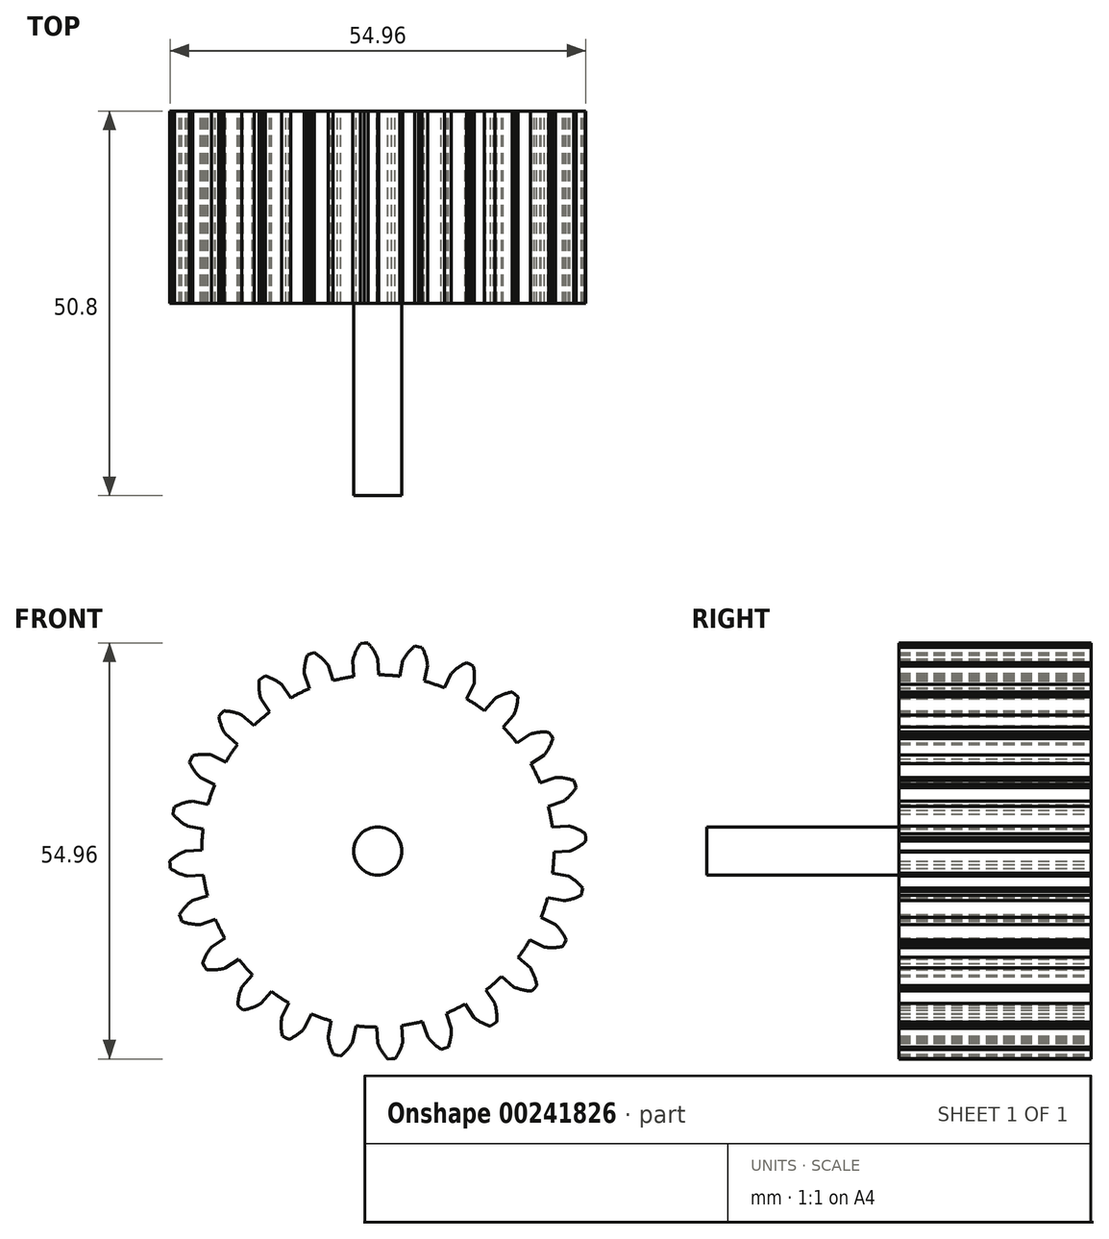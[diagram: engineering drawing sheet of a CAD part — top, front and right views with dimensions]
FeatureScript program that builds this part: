
annotation { "Feature Type Name" : "Feature", "Feature Type Description" : "" }
export const myFeature = defineFeature(function(context is Context, id is Id, definition is map)
    precondition{}
    {
        {
            var Q0;
            Q0=qCreatedBy(makeId("Front.planeOp"),FACE);
            var sketch = newSketch(context, id + "F0", { "sketchPlane" : qUnion([Q0])});
            skCircle(sketch, "E0", {"center": v(0, 0) * mm, "radius": 23.28 * mm});
            skArc(sketch, "E1.trimOffspring", {"start": v(0, 25.4) * mm, "mid": v(-0.55, 26.5) * mm, "end": v(-1.31, 27.48) * mm});
            skLineSegment(sketch, "E2", {"start": v(0, 25.4) * mm, "end": v(0.14, 23.28) * mm});
            skLineSegment(sketch, "E3", {"start": v(-1.31, 27.48) * mm, "end": v(-1.8, 27.46) * mm});
            skLineSegment(sketch, "E4.MirrorCS", {"start": v(-2.28, 27.42) * mm, "end": v(-1.8, 27.46) * mm});
            skArc(sketch, "E5.MirrorCS", {"start": v(-3.32, 25.18) * mm, "mid": v(-2.9, 26.35) * mm, "end": v(-2.28, 27.42) * mm});
            skLineSegment(sketch, "E6.MirrorCS", {"start": v(-3.32, 25.18) * mm, "end": v(-3.18, 23.07) * mm});
            skPoint(sketch, "E7.orphan", {"position": v(-3.01, 20.57) * mm});
            skPoint(sketch, "E8.orphan", {"position": v(0.3, 20.78) * mm});
            skLineSegment(sketch, "E9.1.0", {"start": v(-9.72, 23.47) * mm, "end": v(-9.04, 21.46) * mm});
            skArc(sketch, "E9.1.1", {"start": v(-9.72, 23.47) * mm, "mid": v(-9.63, 24.7) * mm, "end": v(-9.3, 25.9) * mm});
            skLineSegment(sketch, "E9.1.2", {"start": v(-9.3, 25.9) * mm, "end": v(-8.85, 26.06) * mm});
            skLineSegment(sketch, "E9.1.3", {"start": v(-8.38, 26.2) * mm, "end": v(-8.85, 26.06) * mm});
            skArc(sketch, "E9.1.4", {"start": v(-6.57, 24.53) * mm, "mid": v(-7.4, 25.46) * mm, "end": v(-8.38, 26.2) * mm});
            skLineSegment(sketch, "E9.1.5", {"start": v(-6.57, 24.53) * mm, "end": v(-5.9, 22.53) * mm});
            skLineSegment(sketch, "E9.2.0", {"start": v(-15.46, 20.15) * mm, "end": v(-14.28, 18.39) * mm});
            skArc(sketch, "E9.2.1", {"start": v(-15.46, 20.15) * mm, "mid": v(-15.7, 21.37) * mm, "end": v(-15.69, 22.6) * mm});
            skLineSegment(sketch, "E9.2.2", {"start": v(-15.69, 22.6) * mm, "end": v(-15.29, 22.88) * mm});
            skLineSegment(sketch, "E9.2.3", {"start": v(-14.88, 23.15) * mm, "end": v(-15.29, 22.88) * mm});
            skArc(sketch, "E9.2.4", {"start": v(-12.7, 22) * mm, "mid": v(-13.73, 22.68) * mm, "end": v(-14.88, 23.15) * mm});
            skLineSegment(sketch, "E9.2.5", {"start": v(-12.7, 22) * mm, "end": v(-11.52, 20.23) * mm});
            skLineSegment(sketch, "E9.3.0", {"start": v(-20.15, 15.46) * mm, "end": v(-18.56, 14.06) * mm});
            skArc(sketch, "E9.3.1", {"start": v(-20.15, 15.46) * mm, "mid": v(-20.7, 16.58) * mm, "end": v(-21, 17.77) * mm});
            skLineSegment(sketch, "E9.3.2", {"start": v(-21, 17.77) * mm, "end": v(-20.7, 18.15) * mm});
            skLineSegment(sketch, "E9.3.3", {"start": v(-20.36, 18.5) * mm, "end": v(-20.7, 18.15) * mm});
            skArc(sketch, "E9.3.4", {"start": v(-17.96, 17.96) * mm, "mid": v(-19.14, 18.35) * mm, "end": v(-20.36, 18.5) * mm});
            skLineSegment(sketch, "E9.3.5", {"start": v(-17.96, 17.96) * mm, "end": v(-16.37, 16.56) * mm});
            skLineSegment(sketch, "E9.4.0", {"start": v(-23.47, 9.72) * mm, "end": v(-21.56, 8.78) * mm});
            skArc(sketch, "E9.4.1", {"start": v(-23.47, 9.72) * mm, "mid": v(-24.28, 10.66) * mm, "end": v(-24.89, 11.73) * mm});
            skLineSegment(sketch, "E9.4.2", {"start": v(-24.89, 11.73) * mm, "end": v(-24.68, 12.17) * mm});
            skLineSegment(sketch, "E9.4.3", {"start": v(-24.46, 12.6) * mm, "end": v(-24.68, 12.17) * mm});
            skArc(sketch, "E9.4.4", {"start": v(-22, 12.7) * mm, "mid": v(-23.23, 12.77) * mm, "end": v(-24.46, 12.6) * mm});
            skLineSegment(sketch, "E9.4.5", {"start": v(-22, 12.7) * mm, "end": v(-20.1, 11.76) * mm});
            skLineSegment(sketch, "E9.5.0", {"start": v(-25.18, 3.32) * mm, "end": v(-23.1, 2.9) * mm});
            skArc(sketch, "E9.5.1", {"start": v(-25.18, 3.32) * mm, "mid": v(-26.2, 4) * mm, "end": v(-27.08, 4.9) * mm});
            skLineSegment(sketch, "E9.5.2", {"start": v(-27.08, 4.9) * mm, "end": v(-27, 5.37) * mm});
            skLineSegment(sketch, "E9.5.3", {"start": v(-26.89, 5.84) * mm, "end": v(-27, 5.37) * mm});
            skArc(sketch, "E9.5.4", {"start": v(-24.53, 6.57) * mm, "mid": v(-25.75, 6.32) * mm, "end": v(-26.89, 5.84) * mm});
            skLineSegment(sketch, "E9.5.5", {"start": v(-24.53, 6.57) * mm, "end": v(-22.45, 6.16) * mm});
            skLineSegment(sketch, "E9.6.0", {"start": v(-25.18, -3.32) * mm, "end": v(-23.07, -3.18) * mm});
            skArc(sketch, "E9.6.1", {"start": v(-25.18, -3.32) * mm, "mid": v(-26.35, -2.9) * mm, "end": v(-27.42, -2.28) * mm});
            skLineSegment(sketch, "E9.6.2", {"start": v(-27.42, -2.28) * mm, "end": v(-27.46, -1.8) * mm});
            skLineSegment(sketch, "E9.6.3", {"start": v(-27.48, -1.31) * mm, "end": v(-27.46, -1.8) * mm});
            skArc(sketch, "E9.6.4", {"start": v(-25.4, 0) * mm, "mid": v(-26.5, -0.55) * mm, "end": v(-27.48, -1.31) * mm});
            skLineSegment(sketch, "E9.6.5", {"start": v(-25.4, 0) * mm, "end": v(-23.28, 0.14) * mm});
            skLineSegment(sketch, "E9.7.0", {"start": v(-23.47, -9.72) * mm, "end": v(-21.46, -9.04) * mm});
            skArc(sketch, "E9.7.1", {"start": v(-23.47, -9.72) * mm, "mid": v(-24.7, -9.63) * mm, "end": v(-25.9, -9.3) * mm});
            skLineSegment(sketch, "E9.7.2", {"start": v(-25.9, -9.3) * mm, "end": v(-26.06, -8.85) * mm});
            skLineSegment(sketch, "E9.7.3", {"start": v(-26.2, -8.38) * mm, "end": v(-26.06, -8.85) * mm});
            skArc(sketch, "E9.7.4", {"start": v(-24.53, -6.57) * mm, "mid": v(-25.46, -7.4) * mm, "end": v(-26.2, -8.38) * mm});
            skLineSegment(sketch, "E9.7.5", {"start": v(-24.53, -6.57) * mm, "end": v(-22.53, -5.9) * mm});
            skLineSegment(sketch, "E9.8.0", {"start": v(-20.15, -15.46) * mm, "end": v(-18.39, -14.28) * mm});
            skArc(sketch, "E9.8.1", {"start": v(-20.15, -15.46) * mm, "mid": v(-21.37, -15.7) * mm, "end": v(-22.6, -15.69) * mm});
            skLineSegment(sketch, "E9.8.2", {"start": v(-22.6, -15.69) * mm, "end": v(-22.88, -15.29) * mm});
            skLineSegment(sketch, "E9.8.3", {"start": v(-23.15, -14.88) * mm, "end": v(-22.88, -15.29) * mm});
            skArc(sketch, "E9.8.4", {"start": v(-22, -12.7) * mm, "mid": v(-22.68, -13.73) * mm, "end": v(-23.15, -14.88) * mm});
            skLineSegment(sketch, "E9.8.5", {"start": v(-22, -12.7) * mm, "end": v(-20.23, -11.52) * mm});
            skLineSegment(sketch, "E9.9.0", {"start": v(-15.46, -20.15) * mm, "end": v(-14.06, -18.56) * mm});
            skArc(sketch, "E9.9.1", {"start": v(-15.46, -20.15) * mm, "mid": v(-16.58, -20.7) * mm, "end": v(-17.77, -21) * mm});
            skLineSegment(sketch, "E9.9.2", {"start": v(-17.77, -21) * mm, "end": v(-18.15, -20.7) * mm});
            skLineSegment(sketch, "E9.9.3", {"start": v(-18.5, -20.36) * mm, "end": v(-18.15, -20.7) * mm});
            skArc(sketch, "E9.9.4", {"start": v(-17.96, -17.96) * mm, "mid": v(-18.35, -19.14) * mm, "end": v(-18.5, -20.36) * mm});
            skLineSegment(sketch, "E9.9.5", {"start": v(-17.96, -17.96) * mm, "end": v(-16.56, -16.37) * mm});
            skLineSegment(sketch, "E9.10.0", {"start": v(-9.72, -23.47) * mm, "end": v(-8.78, -21.56) * mm});
            skArc(sketch, "E9.10.1", {"start": v(-9.72, -23.47) * mm, "mid": v(-10.66, -24.28) * mm, "end": v(-11.73, -24.89) * mm});
            skLineSegment(sketch, "E9.10.2", {"start": v(-11.73, -24.89) * mm, "end": v(-12.17, -24.68) * mm});
            skLineSegment(sketch, "E9.10.3", {"start": v(-12.6, -24.46) * mm, "end": v(-12.17, -24.68) * mm});
            skArc(sketch, "E9.10.4", {"start": v(-12.7, -22) * mm, "mid": v(-12.77, -23.23) * mm, "end": v(-12.6, -24.46) * mm});
            skLineSegment(sketch, "E9.10.5", {"start": v(-12.7, -22) * mm, "end": v(-11.76, -20.1) * mm});
            skLineSegment(sketch, "E9.11.0", {"start": v(-3.32, -25.18) * mm, "end": v(-2.9, -23.1) * mm});
            skArc(sketch, "E9.11.1", {"start": v(-3.32, -25.18) * mm, "mid": v(-4, -26.2) * mm, "end": v(-4.9, -27.08) * mm});
            skLineSegment(sketch, "E9.11.2", {"start": v(-4.9, -27.08) * mm, "end": v(-5.37, -27) * mm});
            skLineSegment(sketch, "E9.11.3", {"start": v(-5.84, -26.89) * mm, "end": v(-5.37, -27) * mm});
            skArc(sketch, "E9.11.4", {"start": v(-6.57, -24.53) * mm, "mid": v(-6.32, -25.75) * mm, "end": v(-5.84, -26.89) * mm});
            skLineSegment(sketch, "E9.11.5", {"start": v(-6.57, -24.53) * mm, "end": v(-6.16, -22.45) * mm});
            skLineSegment(sketch, "E9.12.0", {"start": v(3.32, -25.18) * mm, "end": v(3.18, -23.07) * mm});
            skArc(sketch, "E9.12.1", {"start": v(3.32, -25.18) * mm, "mid": v(2.9, -26.35) * mm, "end": v(2.28, -27.42) * mm});
            skLineSegment(sketch, "E9.12.2", {"start": v(2.28, -27.42) * mm, "end": v(1.8, -27.46) * mm});
            skLineSegment(sketch, "E9.12.3", {"start": v(1.31, -27.48) * mm, "end": v(1.8, -27.46) * mm});
            skArc(sketch, "E9.12.4", {"start": v(0, -25.4) * mm, "mid": v(0.55, -26.5) * mm, "end": v(1.31, -27.48) * mm});
            skLineSegment(sketch, "E9.12.5", {"start": v(0, -25.4) * mm, "end": v(-0.14, -23.28) * mm});
            skLineSegment(sketch, "E9.13.0", {"start": v(9.72, -23.47) * mm, "end": v(9.04, -21.46) * mm});
            skArc(sketch, "E9.13.1", {"start": v(9.72, -23.47) * mm, "mid": v(9.63, -24.7) * mm, "end": v(9.3, -25.9) * mm});
            skLineSegment(sketch, "E9.13.2", {"start": v(9.3, -25.9) * mm, "end": v(8.85, -26.06) * mm});
            skLineSegment(sketch, "E9.13.3", {"start": v(8.38, -26.2) * mm, "end": v(8.85, -26.06) * mm});
            skArc(sketch, "E9.13.4", {"start": v(6.57, -24.53) * mm, "mid": v(7.4, -25.46) * mm, "end": v(8.38, -26.2) * mm});
            skLineSegment(sketch, "E9.13.5", {"start": v(6.57, -24.53) * mm, "end": v(5.9, -22.53) * mm});
            skLineSegment(sketch, "E9.14.0", {"start": v(15.46, -20.15) * mm, "end": v(14.28, -18.39) * mm});
            skArc(sketch, "E9.14.1", {"start": v(15.46, -20.15) * mm, "mid": v(15.7, -21.37) * mm, "end": v(15.69, -22.6) * mm});
            skLineSegment(sketch, "E9.14.2", {"start": v(15.69, -22.6) * mm, "end": v(15.29, -22.88) * mm});
            skLineSegment(sketch, "E9.14.3", {"start": v(14.88, -23.15) * mm, "end": v(15.29, -22.88) * mm});
            skArc(sketch, "E9.14.4", {"start": v(12.7, -22) * mm, "mid": v(13.73, -22.68) * mm, "end": v(14.88, -23.15) * mm});
            skLineSegment(sketch, "E9.14.5", {"start": v(12.7, -22) * mm, "end": v(11.52, -20.23) * mm});
            skLineSegment(sketch, "E9.15.0", {"start": v(20.15, -15.46) * mm, "end": v(18.56, -14.06) * mm});
            skArc(sketch, "E9.15.1", {"start": v(20.15, -15.46) * mm, "mid": v(20.7, -16.58) * mm, "end": v(21, -17.77) * mm});
            skLineSegment(sketch, "E9.15.2", {"start": v(21, -17.77) * mm, "end": v(20.7, -18.15) * mm});
            skLineSegment(sketch, "E9.15.3", {"start": v(20.36, -18.5) * mm, "end": v(20.7, -18.15) * mm});
            skArc(sketch, "E9.15.4", {"start": v(17.96, -17.96) * mm, "mid": v(19.14, -18.35) * mm, "end": v(20.36, -18.5) * mm});
            skLineSegment(sketch, "E9.15.5", {"start": v(17.96, -17.96) * mm, "end": v(16.37, -16.56) * mm});
            skLineSegment(sketch, "E9.16.0", {"start": v(23.47, -9.72) * mm, "end": v(21.56, -8.78) * mm});
            skArc(sketch, "E9.16.1", {"start": v(23.47, -9.72) * mm, "mid": v(24.28, -10.66) * mm, "end": v(24.89, -11.73) * mm});
            skLineSegment(sketch, "E9.16.2", {"start": v(24.89, -11.73) * mm, "end": v(24.68, -12.17) * mm});
            skLineSegment(sketch, "E9.16.3", {"start": v(24.46, -12.6) * mm, "end": v(24.68, -12.17) * mm});
            skArc(sketch, "E9.16.4", {"start": v(22, -12.7) * mm, "mid": v(23.23, -12.77) * mm, "end": v(24.46, -12.6) * mm});
            skLineSegment(sketch, "E9.16.5", {"start": v(22, -12.7) * mm, "end": v(20.1, -11.76) * mm});
            skLineSegment(sketch, "E9.17.0", {"start": v(25.18, -3.32) * mm, "end": v(23.1, -2.9) * mm});
            skArc(sketch, "E9.17.1", {"start": v(25.18, -3.32) * mm, "mid": v(26.2, -4) * mm, "end": v(27.08, -4.9) * mm});
            skLineSegment(sketch, "E9.17.2", {"start": v(27.08, -4.9) * mm, "end": v(27, -5.37) * mm});
            skLineSegment(sketch, "E9.17.3", {"start": v(26.89, -5.84) * mm, "end": v(27, -5.37) * mm});
            skArc(sketch, "E9.17.4", {"start": v(24.53, -6.57) * mm, "mid": v(25.75, -6.32) * mm, "end": v(26.89, -5.84) * mm});
            skLineSegment(sketch, "E9.17.5", {"start": v(24.53, -6.57) * mm, "end": v(22.45, -6.16) * mm});
            skLineSegment(sketch, "E9.18.0", {"start": v(25.18, 3.32) * mm, "end": v(23.07, 3.18) * mm});
            skArc(sketch, "E9.18.1", {"start": v(25.18, 3.32) * mm, "mid": v(26.35, 2.9) * mm, "end": v(27.42, 2.28) * mm});
            skLineSegment(sketch, "E9.18.2", {"start": v(27.42, 2.28) * mm, "end": v(27.46, 1.8) * mm});
            skLineSegment(sketch, "E9.18.3", {"start": v(27.48, 1.31) * mm, "end": v(27.46, 1.8) * mm});
            skArc(sketch, "E9.18.4", {"start": v(25.4, 0) * mm, "mid": v(26.5, 0.55) * mm, "end": v(27.48, 1.31) * mm});
            skLineSegment(sketch, "E9.18.5", {"start": v(25.4, 0) * mm, "end": v(23.28, -0.14) * mm});
            skLineSegment(sketch, "E9.19.0", {"start": v(23.47, 9.72) * mm, "end": v(21.46, 9.04) * mm});
            skArc(sketch, "E9.19.1", {"start": v(23.47, 9.72) * mm, "mid": v(24.7, 9.63) * mm, "end": v(25.9, 9.3) * mm});
            skLineSegment(sketch, "E9.19.2", {"start": v(25.9, 9.3) * mm, "end": v(26.06, 8.85) * mm});
            skLineSegment(sketch, "E9.19.3", {"start": v(26.2, 8.38) * mm, "end": v(26.06, 8.85) * mm});
            skArc(sketch, "E9.19.4", {"start": v(24.53, 6.57) * mm, "mid": v(25.46, 7.4) * mm, "end": v(26.2, 8.38) * mm});
            skLineSegment(sketch, "E9.19.5", {"start": v(24.53, 6.57) * mm, "end": v(22.53, 5.9) * mm});
            skLineSegment(sketch, "E9.20.0", {"start": v(20.15, 15.46) * mm, "end": v(18.39, 14.28) * mm});
            skArc(sketch, "E9.20.1", {"start": v(20.15, 15.46) * mm, "mid": v(21.37, 15.7) * mm, "end": v(22.6, 15.69) * mm});
            skLineSegment(sketch, "E9.20.2", {"start": v(22.6, 15.69) * mm, "end": v(22.88, 15.29) * mm});
            skLineSegment(sketch, "E9.20.3", {"start": v(23.15, 14.88) * mm, "end": v(22.88, 15.29) * mm});
            skArc(sketch, "E9.20.4", {"start": v(22, 12.7) * mm, "mid": v(22.68, 13.73) * mm, "end": v(23.15, 14.88) * mm});
            skLineSegment(sketch, "E9.20.5", {"start": v(22, 12.7) * mm, "end": v(20.23, 11.52) * mm});
            skLineSegment(sketch, "E9.21.0", {"start": v(15.46, 20.15) * mm, "end": v(14.06, 18.56) * mm});
            skArc(sketch, "E9.21.1", {"start": v(15.46, 20.15) * mm, "mid": v(16.58, 20.7) * mm, "end": v(17.77, 21) * mm});
            skLineSegment(sketch, "E9.21.2", {"start": v(17.77, 21) * mm, "end": v(18.15, 20.7) * mm});
            skLineSegment(sketch, "E9.21.3", {"start": v(18.5, 20.36) * mm, "end": v(18.15, 20.7) * mm});
            skArc(sketch, "E9.21.4", {"start": v(17.96, 17.96) * mm, "mid": v(18.35, 19.14) * mm, "end": v(18.5, 20.36) * mm});
            skLineSegment(sketch, "E9.21.5", {"start": v(17.96, 17.96) * mm, "end": v(16.56, 16.37) * mm});
            skLineSegment(sketch, "E9.22.0", {"start": v(9.72, 23.47) * mm, "end": v(8.78, 21.56) * mm});
            skArc(sketch, "E9.22.1", {"start": v(9.72, 23.47) * mm, "mid": v(10.66, 24.28) * mm, "end": v(11.73, 24.89) * mm});
            skLineSegment(sketch, "E9.22.2", {"start": v(11.73, 24.89) * mm, "end": v(12.17, 24.68) * mm});
            skLineSegment(sketch, "E9.22.3", {"start": v(12.6, 24.46) * mm, "end": v(12.17, 24.68) * mm});
            skArc(sketch, "E9.22.4", {"start": v(12.7, 22) * mm, "mid": v(12.77, 23.23) * mm, "end": v(12.6, 24.46) * mm});
            skLineSegment(sketch, "E9.22.5", {"start": v(12.7, 22) * mm, "end": v(11.76, 20.1) * mm});
            skLineSegment(sketch, "E9.23.0", {"start": v(3.32, 25.18) * mm, "end": v(2.9, 23.1) * mm});
            skArc(sketch, "E9.23.1", {"start": v(3.32, 25.18) * mm, "mid": v(4, 26.2) * mm, "end": v(4.9, 27.08) * mm});
            skLineSegment(sketch, "E9.23.2", {"start": v(4.9, 27.08) * mm, "end": v(5.37, 27) * mm});
            skLineSegment(sketch, "E9.23.3", {"start": v(5.84, 26.89) * mm, "end": v(5.37, 27) * mm});
            skArc(sketch, "E9.23.4", {"start": v(6.57, 24.53) * mm, "mid": v(6.32, 25.75) * mm, "end": v(5.84, 26.89) * mm});
            skLineSegment(sketch, "E9.23.5", {"start": v(6.57, 24.53) * mm, "end": v(6.16, 22.45) * mm});
            skSolve(sketch);
        }
        {
            var Q0;
            Q0 = qSketchRegion(id + "F0", true);
            extrude(context, id + "F1", {"entities" : qUnion([Q0]), "depth" : 25.4 * mm});
        }
        {
            var Q0;
            Q0=makeQuery(id+"F1.opExtrude","CAP_FACE",FACE,{"disambiguationData":[OSD([sQuery(id+"F0.wireOp",EDGE,"E0"),sQuery(id+"F0.wireOp",EDGE,"E1.trimOffspring"),sQuery(id+"F0.wireOp",EDGE,"E2"),sQuery(id+"F0.wireOp",EDGE,"E3"),sQuery(id+"F0.wireOp",EDGE,"E4.MirrorCS"),sQuery(id+"F0.wireOp",EDGE,"E5.MirrorCS"),sQuery(id+"F0.wireOp",EDGE,"E6.MirrorCS"),sQuery(id+"F0.wireOp",EDGE,"E9.1.0"),sQuery(id+"F0.wireOp",EDGE,"E9.1.1"),sQuery(id+"F0.wireOp",EDGE,"E9.1.2"),sQuery(id+"F0.wireOp",EDGE,"E9.1.3"),sQuery(id+"F0.wireOp",EDGE,"E9.1.4"),sQuery(id+"F0.wireOp",EDGE,"E9.1.5"),sQuery(id+"F0.wireOp",EDGE,"E9.2.0"),sQuery(id+"F0.wireOp",EDGE,"E9.2.1"),sQuery(id+"F0.wireOp",EDGE,"E9.2.2"),sQuery(id+"F0.wireOp",EDGE,"E9.2.3"),sQuery(id+"F0.wireOp",EDGE,"E9.2.4"),sQuery(id+"F0.wireOp",EDGE,"E9.2.5"),sQuery(id+"F0.wireOp",EDGE,"E9.3.0"),sQuery(id+"F0.wireOp",EDGE,"E9.3.1"),sQuery(id+"F0.wireOp",EDGE,"E9.3.2"),sQuery(id+"F0.wireOp",EDGE,"E9.3.3"),sQuery(id+"F0.wireOp",EDGE,"E9.3.4"),sQuery(id+"F0.wireOp",EDGE,"E9.3.5"),sQuery(id+"F0.wireOp",EDGE,"E9.4.0"),sQuery(id+"F0.wireOp",EDGE,"E9.4.1"),sQuery(id+"F0.wireOp",EDGE,"E9.4.2"),sQuery(id+"F0.wireOp",EDGE,"E9.4.3"),sQuery(id+"F0.wireOp",EDGE,"E9.4.4"),sQuery(id+"F0.wireOp",EDGE,"E9.4.5"),sQuery(id+"F0.wireOp",EDGE,"E9.5.0"),sQuery(id+"F0.wireOp",EDGE,"E9.5.1"),sQuery(id+"F0.wireOp",EDGE,"E9.5.2"),sQuery(id+"F0.wireOp",EDGE,"E9.5.3"),sQuery(id+"F0.wireOp",EDGE,"E9.5.4"),sQuery(id+"F0.wireOp",EDGE,"E9.5.5"),sQuery(id+"F0.wireOp",EDGE,"E9.6.0"),sQuery(id+"F0.wireOp",EDGE,"E9.6.1"),sQuery(id+"F0.wireOp",EDGE,"E9.6.2"),sQuery(id+"F0.wireOp",EDGE,"E9.6.3"),sQuery(id+"F0.wireOp",EDGE,"E9.6.4"),sQuery(id+"F0.wireOp",EDGE,"E9.6.5"),sQuery(id+"F0.wireOp",EDGE,"E9.7.0"),sQuery(id+"F0.wireOp",EDGE,"E9.7.1"),sQuery(id+"F0.wireOp",EDGE,"E9.7.2"),sQuery(id+"F0.wireOp",EDGE,"E9.7.3"),sQuery(id+"F0.wireOp",EDGE,"E9.7.4"),sQuery(id+"F0.wireOp",EDGE,"E9.7.5"),sQuery(id+"F0.wireOp",EDGE,"E9.8.0"),sQuery(id+"F0.wireOp",EDGE,"E9.8.1"),sQuery(id+"F0.wireOp",EDGE,"E9.8.2"),sQuery(id+"F0.wireOp",EDGE,"E9.8.3"),sQuery(id+"F0.wireOp",EDGE,"E9.8.4"),sQuery(id+"F0.wireOp",EDGE,"E9.8.5"),sQuery(id+"F0.wireOp",EDGE,"E9.9.0"),sQuery(id+"F0.wireOp",EDGE,"E9.9.1"),sQuery(id+"F0.wireOp",EDGE,"E9.9.2"),sQuery(id+"F0.wireOp",EDGE,"E9.9.3"),sQuery(id+"F0.wireOp",EDGE,"E9.9.4"),sQuery(id+"F0.wireOp",EDGE,"E9.9.5"),sQuery(id+"F0.wireOp",EDGE,"E9.10.0"),sQuery(id+"F0.wireOp",EDGE,"E9.10.1"),sQuery(id+"F0.wireOp",EDGE,"E9.10.2"),sQuery(id+"F0.wireOp",EDGE,"E9.10.3"),sQuery(id+"F0.wireOp",EDGE,"E9.10.4"),sQuery(id+"F0.wireOp",EDGE,"E9.10.5"),sQuery(id+"F0.wireOp",EDGE,"E9.11.0"),sQuery(id+"F0.wireOp",EDGE,"E9.11.1"),sQuery(id+"F0.wireOp",EDGE,"E9.11.2"),sQuery(id+"F0.wireOp",EDGE,"E9.11.3"),sQuery(id+"F0.wireOp",EDGE,"E9.11.4"),sQuery(id+"F0.wireOp",EDGE,"E9.11.5"),sQuery(id+"F0.wireOp",EDGE,"E9.12.0"),sQuery(id+"F0.wireOp",EDGE,"E9.12.1"),sQuery(id+"F0.wireOp",EDGE,"E9.12.2"),sQuery(id+"F0.wireOp",EDGE,"E9.12.3"),sQuery(id+"F0.wireOp",EDGE,"E9.12.4"),sQuery(id+"F0.wireOp",EDGE,"E9.12.5"),sQuery(id+"F0.wireOp",EDGE,"E9.13.0"),sQuery(id+"F0.wireOp",EDGE,"E9.13.1"),sQuery(id+"F0.wireOp",EDGE,"E9.13.2"),sQuery(id+"F0.wireOp",EDGE,"E9.13.3"),sQuery(id+"F0.wireOp",EDGE,"E9.13.4"),sQuery(id+"F0.wireOp",EDGE,"E9.13.5"),sQuery(id+"F0.wireOp",EDGE,"E9.14.0"),sQuery(id+"F0.wireOp",EDGE,"E9.14.1"),sQuery(id+"F0.wireOp",EDGE,"E9.14.2"),sQuery(id+"F0.wireOp",EDGE,"E9.14.3"),sQuery(id+"F0.wireOp",EDGE,"E9.14.4"),sQuery(id+"F0.wireOp",EDGE,"E9.14.5"),sQuery(id+"F0.wireOp",EDGE,"E9.15.0"),sQuery(id+"F0.wireOp",EDGE,"E9.15.1"),sQuery(id+"F0.wireOp",EDGE,"E9.15.2"),sQuery(id+"F0.wireOp",EDGE,"E9.15.3"),sQuery(id+"F0.wireOp",EDGE,"E9.15.4"),sQuery(id+"F0.wireOp",EDGE,"E9.15.5"),sQuery(id+"F0.wireOp",EDGE,"E9.16.0"),sQuery(id+"F0.wireOp",EDGE,"E9.16.1"),sQuery(id+"F0.wireOp",EDGE,"E9.16.2"),sQuery(id+"F0.wireOp",EDGE,"E9.16.3"),sQuery(id+"F0.wireOp",EDGE,"E9.16.4"),sQuery(id+"F0.wireOp",EDGE,"E9.16.5"),sQuery(id+"F0.wireOp",EDGE,"E9.17.0"),sQuery(id+"F0.wireOp",EDGE,"E9.17.1"),sQuery(id+"F0.wireOp",EDGE,"E9.17.2"),sQuery(id+"F0.wireOp",EDGE,"E9.17.3"),sQuery(id+"F0.wireOp",EDGE,"E9.17.4"),sQuery(id+"F0.wireOp",EDGE,"E9.17.5"),sQuery(id+"F0.wireOp",EDGE,"E9.18.0"),sQuery(id+"F0.wireOp",EDGE,"E9.18.1"),sQuery(id+"F0.wireOp",EDGE,"E9.18.2"),sQuery(id+"F0.wireOp",EDGE,"E9.18.3"),sQuery(id+"F0.wireOp",EDGE,"E9.18.4"),sQuery(id+"F0.wireOp",EDGE,"E9.18.5"),sQuery(id+"F0.wireOp",EDGE,"E9.19.0"),sQuery(id+"F0.wireOp",EDGE,"E9.19.1"),sQuery(id+"F0.wireOp",EDGE,"E9.19.2"),sQuery(id+"F0.wireOp",EDGE,"E9.19.3"),sQuery(id+"F0.wireOp",EDGE,"E9.19.4"),sQuery(id+"F0.wireOp",EDGE,"E9.19.5"),sQuery(id+"F0.wireOp",EDGE,"E9.20.0"),sQuery(id+"F0.wireOp",EDGE,"E9.20.1"),sQuery(id+"F0.wireOp",EDGE,"E9.20.2"),sQuery(id+"F0.wireOp",EDGE,"E9.20.3"),sQuery(id+"F0.wireOp",EDGE,"E9.20.4"),sQuery(id+"F0.wireOp",EDGE,"E9.20.5"),sQuery(id+"F0.wireOp",EDGE,"E9.21.0"),sQuery(id+"F0.wireOp",EDGE,"E9.21.1"),sQuery(id+"F0.wireOp",EDGE,"E9.21.2"),sQuery(id+"F0.wireOp",EDGE,"E9.21.3"),sQuery(id+"F0.wireOp",EDGE,"E9.21.4"),sQuery(id+"F0.wireOp",EDGE,"E9.21.5"),sQuery(id+"F0.wireOp",EDGE,"E9.22.0"),sQuery(id+"F0.wireOp",EDGE,"E9.22.1"),sQuery(id+"F0.wireOp",EDGE,"E9.22.2"),sQuery(id+"F0.wireOp",EDGE,"E9.22.3"),sQuery(id+"F0.wireOp",EDGE,"E9.22.4"),sQuery(id+"F0.wireOp",EDGE,"E9.22.5"),sQuery(id+"F0.wireOp",EDGE,"E9.23.0"),sQuery(id+"F0.wireOp",EDGE,"E9.23.1"),sQuery(id+"F0.wireOp",EDGE,"E9.23.2"),sQuery(id+"F0.wireOp",EDGE,"E9.23.3"),sQuery(id+"F0.wireOp",EDGE,"E9.23.4"),sQuery(id+"F0.wireOp",EDGE,"E9.23.5")])],"isStart":false});
            var sketch = newSketch(context, id + "F2", { "sketchPlane" : qUnion([Q0])});
            skCircle(sketch, "E10", {"center": v(0, 0) * mm, "radius": 3.17 * mm});
            skSolve(sketch);
        }
        {
            var Q0;
            Q0 = qSketchRegion(id + "F2", true);
            extrude(context, id + "F3", {"entities" : qUnion([Q0]), "operationType" : NewBodyOperationType.ADD, "depth" : 25.4 * mm});
        }
    });
